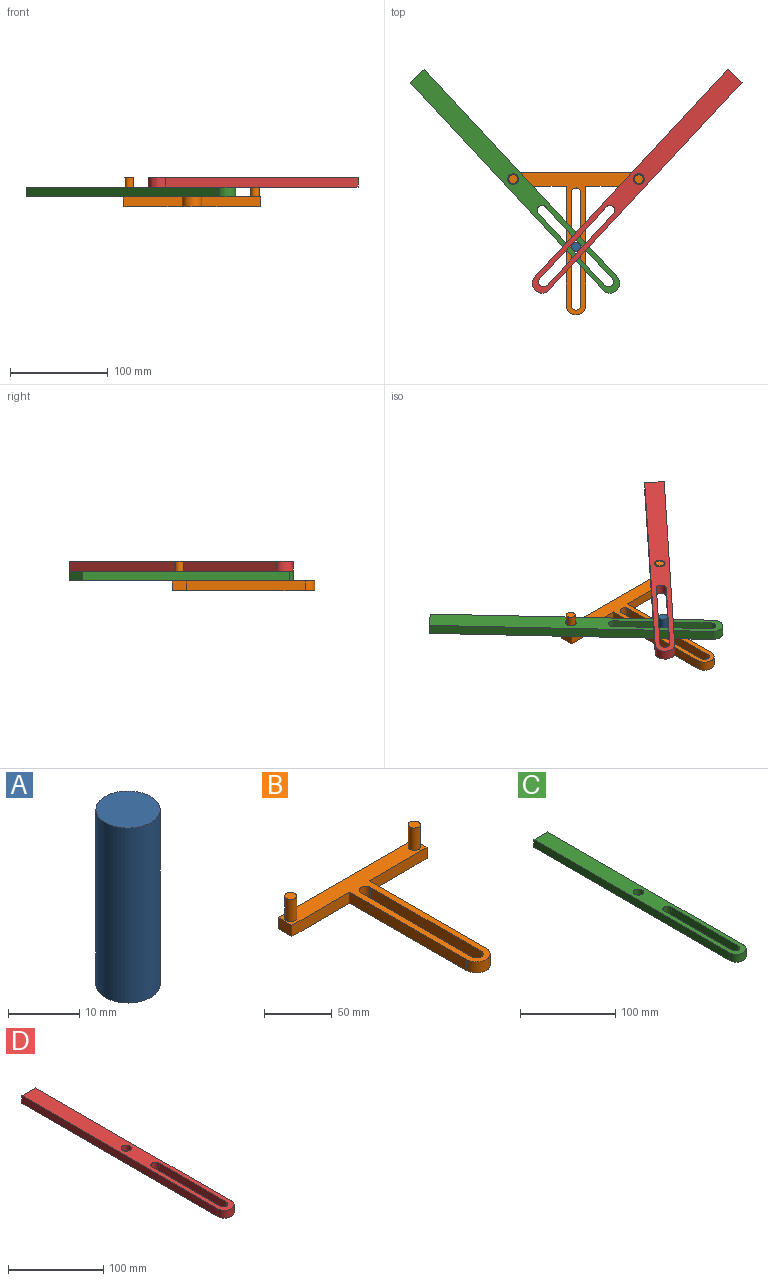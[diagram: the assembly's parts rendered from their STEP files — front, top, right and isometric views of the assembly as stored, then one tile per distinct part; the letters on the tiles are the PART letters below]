
ASSEMBLY  parts=4 mates=5
PART A: 3 faces, bbox 9x9x30 mm
  f0: cylinder r=4.5mm len=30mm, axis (0,0,-1), area 848.2mm2, adj f1,f2
  f1: plane 9x9mm, normal (0,0,1), area 63.6mm2, adj f0
  f2: plane 9x9mm, normal (0,0,-1), area 63.6mm2, adj f0
PART B: 18 faces, bbox 140.7x146.2x30 mm
  f0: plane 60.34x10mm, normal (0,-1,0), area 603.4mm2, adj f1,f5,f6,f11
  f1: plane 14.42x10mm, normal (1,0,0), area 144.2mm2, adj f0,f2,f5,f6
  f2: plane 140.67x10mm, normal (0,1,0), area 1406.7mm2, adj f1,f3,f5,f6
  f3: plane 14.42x10mm, normal (-1,0,0), area 144.2mm2, adj f2,f4,f5,f6
  f4: plane 60.34x10mm, normal (0,-1,0), area 603.4mm2, adj f3,f5,f6,f12
  f5: plane 146.21x140.67mm, normal (0,0,-1), area 3393mm2, adj f0,f1,f2,f3,f4,f11,f12,f13
  f6: plane 146.21x140.67mm, normal (0,0,1), area 3265.7mm2, adj f0,f1,f2,f3,f4,f7,f9,f11
  f7: cylinder r=4.5mm len=20mm, axis (0,0,-1), area 565.5mm2, adj f6,f8
  f8: plane 9x9mm, normal (0,0,1), area 63.6mm2, adj f7
  f9: cylinder r=4.5mm len=20mm, axis (0,0,-1), area 565.5mm2, adj f6,f10
  f10: plane 9x9mm, normal (0,0,1), area 63.6mm2, adj f9
  f11: plane 121.79x10mm, normal (1,0,0), area 1217.9mm2, adj f0,f5,f6,f17
  f12: plane 121.79x10mm, normal (-1,0,0), area 1217.9mm2, adj f4,f5,f6,f17
  f13: plane 115x10mm, normal (-1,0,0), area 1150mm2, adj f5,f6,f14,f16
  f14: cylinder r=5mm len=10mm, axis (0,0,1), area 157.1mm2, adj f5,f6,f13,f15
  f15: plane 115x10mm, normal (1,0,0), area 1150mm2, adj f5,f6,f14,f16
  f16: cylinder r=5mm len=10mm, axis (0,0,1), area 157.1mm2, adj f5,f6,f13,f15
  f17: cylinder r=10mm len=20mm, axis (0,0,1), area 314.2mm2, adj f5,f6,f11,f12
PART C: 11 faces, bbox 20x300x10 mm
  f0: cylinder r=5mm len=10mm, axis (0,0,-1), area 157.1mm2, adj f1,f6,f8,f9
  f1: plane 100x10mm, normal (1,0,0), area 1000mm2, adj f0,f2,f8,f9
  f2: cylinder r=5mm len=10mm, axis (0,0,-1), area 157.1mm2, adj f1,f6,f8,f9
  f3: plane 290x10mm, normal (1,0,0), area 2900mm2, adj f4,f8,f9,f10
  f4: plane 20x10mm, normal (0,1,0), area 200mm2, adj f3,f5,f8,f9
  f5: plane 290x10mm, normal (-1,0,0), area 2900mm2, adj f4,f8,f9,f10
  f6: plane 100x10mm, normal (-1,0,0), area 1000mm2, adj f0,f2,f8,f9
  f7: cylinder r=5.5mm len=11mm, axis (0,0,-1), area 345.6mm2, adj f8,f9
  f8: plane 300x20mm, normal (0,0,1), area 4783.5mm2, adj f0,f1,f2,f3,f4,f5,f6,f7
  f9: plane 300x20mm, normal (0,0,-1), area 4783.5mm2, adj f0,f1,f2,f3,f4,f5,f6,f7
  f10: cylinder r=10mm len=20mm, axis (0,0,1), area 314.2mm2, adj f3,f5,f8,f9
PART D: 11 faces, bbox 20x300x10 mm
  f0: cylinder r=5mm len=10mm, axis (0,0,-1), area 157.1mm2, adj f1,f6,f8,f9
  f1: plane 100x10mm, normal (-1,0,0), area 1000mm2, adj f0,f2,f8,f9
  f2: cylinder r=5mm len=10mm, axis (0,0,-1), area 157.1mm2, adj f1,f6,f8,f9
  f3: plane 290x10mm, normal (-1,0,0), area 2900mm2, adj f4,f8,f9,f10
  f4: plane 20x10mm, normal (0,1,0), area 200mm2, adj f3,f5,f8,f9
  f5: plane 290x10mm, normal (1,0,0), area 2900mm2, adj f4,f8,f9,f10
  f6: plane 100x10mm, normal (1,0,0), area 1000mm2, adj f0,f2,f8,f9
  f7: cylinder r=5.5mm len=11mm, axis (0,0,-1), area 345.6mm2, adj f8,f9
  f8: plane 300x20mm, normal (0,0,1), area 4783.5mm2, adj f0,f1,f2,f3,f4,f5,f6,f7
  f9: plane 300x20mm, normal (0,0,-1), area 4783.5mm2, adj f0,f1,f2,f3,f4,f5,f6,f7
  f10: cylinder r=10mm len=20mm, axis (0,0,1), area 314.2mm2, adj f3,f5,f8,f9
PLACE A rot(axis=(0,0,-1),90deg) t=(72.56,-62.63,1.44)mm
PLACE B t=(2.48,6.71,-3.56)mm fixed
PLACE C rot(axis=(0,0,1),42.9deg) t=(-14.7,50.47,-3.56)mm
PLACE D rot(axis=(0,0,-1),42.9deg) t=(19.65,50.47,6.44)mm
MATE revolute C.f7 <-> B.f7  axis (0,0,1) through (-61.86,6.71,-3.56)mm
MATE pin_slot A.f0 <-> C.f2  axis (0,0,-1) through (2.48,-62.63,1.44)mm
MATE revolute B.f9 <-> D.f7  axis (0,0,1) through (66.81,6.71,-3.56)mm
MATE pin_slot A.f0 <-> B.f16  axis (0,0,-1) through (2.48,-62.63,-13.56)mm
MATE pin_slot A.f0 <-> D.f2  axis (0,0,1) through (2.48,-62.63,16.44)mm
